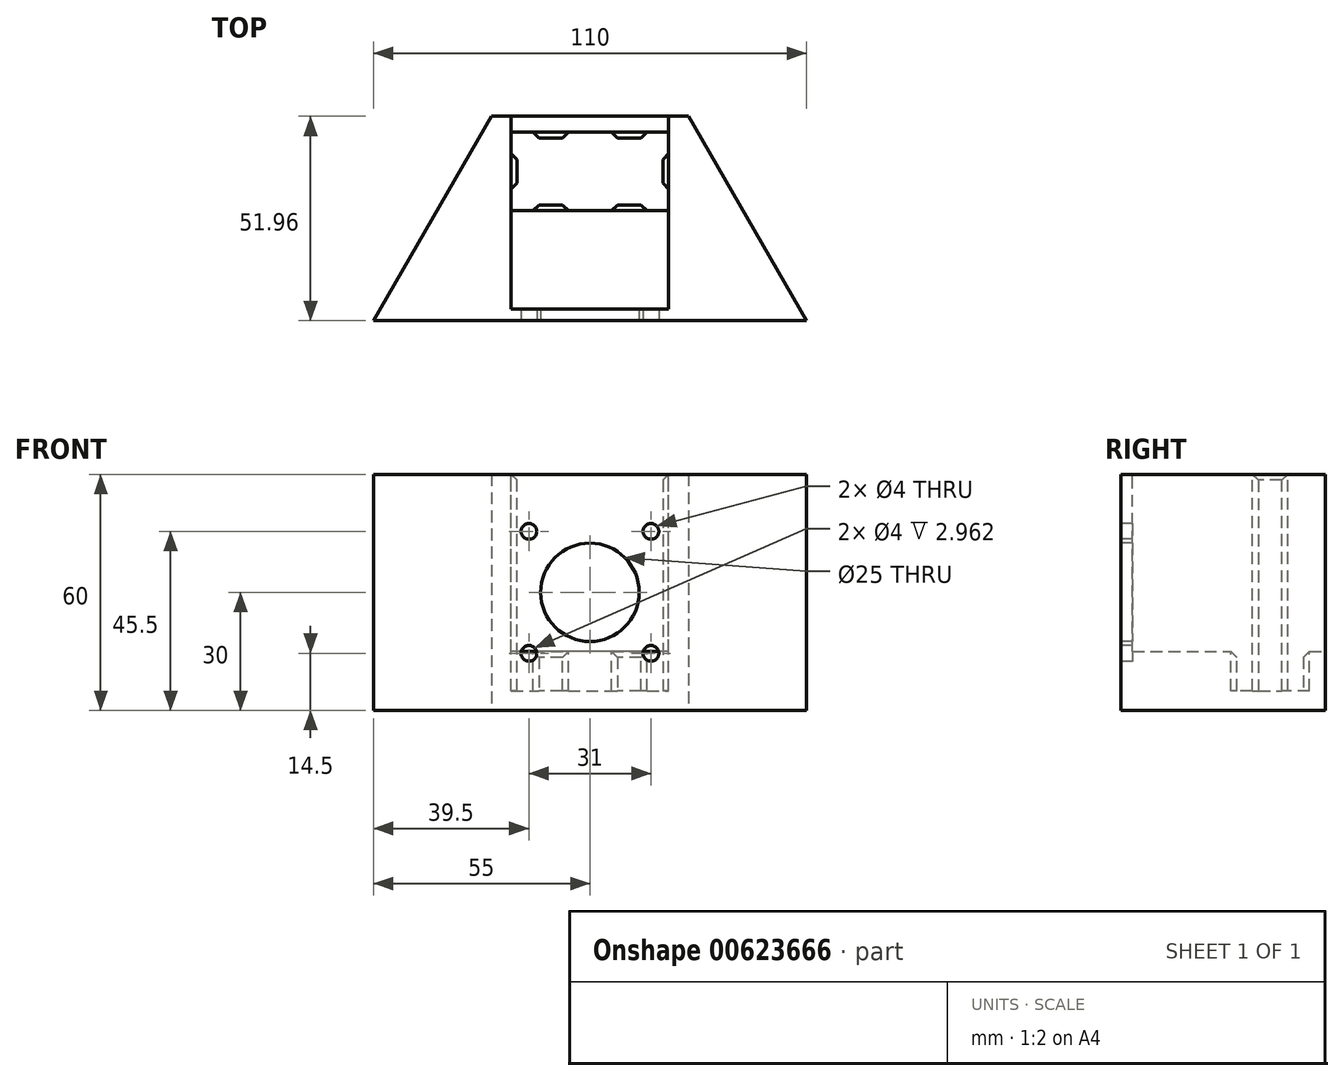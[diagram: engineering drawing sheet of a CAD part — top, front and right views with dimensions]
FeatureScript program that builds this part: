
annotation { "Feature Type Name" : "Feature", "Feature Type Description" : "" }
export const myFeature = defineFeature(function(context is Context, id is Id, definition is map)
    precondition{}
    {
        {
            var Q0;
            Q0=qCreatedBy(makeId("Top.planeOp"),FACE);
            var sketch = newSketch(context, id + "F0", { "sketchPlane" : qUnion([Q0])});
            skLineSegment(sketch, "E0", {"start": v(0, 0) * mm, "end": v(30, 51.96) * mm});
            skLineSegment(sketch, "E1", {"start": v(30, 51.96) * mm, "end": v(80, 51.96) * mm});
            skLineSegment(sketch, "E2", {"start": v(80, 51.96) * mm, "end": v(110, 0) * mm});
            skLineSegment(sketch, "E3", {"start": v(110, 0) * mm, "end": v(0, 0) * mm});
            skSolve(sketch);
        }
        {
            var Q0;
            Q0=makeQuery(id+"F0.imprint","IMPRINT",FACE,{"disambiguationData":[TD([[makeQuery(id+"F0.imprint","IMPRINT",EDGE,{"derivedFrom":sQuery(id+"F0.wireOp",EDGE,"E0")}),-1.0]])]});
            extrude(context, id + "F1", {"entities" : qUnion([Q0]), "depth" : 60 * mm, "offsetDistance" : 25 * mm});
        }
        {
            var Q0;
            Q0=makeQuery(id+"F1.opExtrude","CAP_FACE",FACE,{"disambiguationData":[OSD([sQuery(id+"F0.wireOp",EDGE,"E0"),sQuery(id+"F0.wireOp",EDGE,"E1"),sQuery(id+"F0.wireOp",EDGE,"E2"),sQuery(id+"F0.wireOp",EDGE,"E3")])],"isStart":false});
            var sketch = newSketch(context, id + "F2", { "sketchPlane" : qUnion([Q0])});
            skLineSegment(sketch, "E4.bottom", {"start": v(35, 47.96) * mm, "end": v(75, 47.96) * mm});
            skLineSegment(sketch, "E4.top", {"start": v(35, 27.96) * mm, "end": v(75, 27.96) * mm});
            skLineSegment(sketch, "E4.left", {"start": v(35, 47.96) * mm, "end": v(35, 27.96) * mm});
            skLineSegment(sketch, "E4.right", {"start": v(75, 47.96) * mm, "end": v(75, 27.96) * mm});
            skSolve(sketch);
        }
        {
            var Q0;
            Q0=makeQuery(id+"F2.imprint","IMPRINT",FACE,{"disambiguationData":[TD([[makeQuery(id+"F2.imprint","IMPRINT",EDGE,{"derivedFrom":sQuery(id+"F2.wireOp",EDGE,"E4.bottom")}),-1.0]])]});
            extrude(context, id + "F3", {"entities" : qUnion([Q0]), "operationType" : NewBodyOperationType.REMOVE, "oppositeDirection" : true, "depth" : 55 * mm, "offsetDistance" : 25 * mm});
        }
        {
            var Q0;
            Q0=makeQuery(id+"F1.opExtrude","SWEPT_FACE",FACE,{"disambiguationData":[OSD([sQuery(id+"F0.wireOp",EDGE,"E1")])]});
            var sketch = newSketch(context, id + "F4", { "sketchPlane" : qUnion([Q0])});
            skLineSegment(sketch, "E5.0.0", {"start": v(-35, 60) * mm, "end": v(-75, 60) * mm});
            skLineSegment(sketch, "E5.0.1", {"start": v(-75, 60) * mm, "end": v(-75, 15) * mm});
            skLineSegment(sketch, "E5.0.3", {"start": v(-35, 15) * mm, "end": v(-35, 60) * mm});
            skLineSegment(sketch, "E6", {"start": v(-75, 15) * mm, "end": v(-35, 15) * mm});
            skPoint(sketch, "E7.orphan", {"position": v(-35, 5) * mm});
            skPoint(sketch, "E8.orphan", {"position": v(-75, 5) * mm});
            skSolve(sketch);
        }
        {
            var Q0;
            Q0 = qSketchRegion(id + "F4", true);
            extrude(context, id + "F5", {"entities" : qUnion([Q0]), "operationType" : NewBodyOperationType.REMOVE, "endBound" : BoundingType.UP_TO_NEXT, "oppositeDirection" : true, "depth" : 25 * mm, "offsetDistance" : 25 * mm});
        }
        {
            var Q0;
            Q0=makeQuery(id+"F3.boolean.opBoolean","COPY",FACE,{"derivedFrom":makeQuery(id+"F3.opExtrude","SWEPT_FACE",FACE,{"disambiguationData":[OSD([sQuery(id+"F2.wireOp",EDGE,"E4.top")])]})});
            var sketch = newSketch(context, id + "F6", { "sketchPlane" : qUnion([Q0])});
            skLineSegment(sketch, "E9.0", {"start": v(-35, 60) * mm, "end": v(-75, 60) * mm});
            skLineSegment(sketch, "E10.0", {"start": v(-75, 60) * mm, "end": v(-75, 15) * mm});
            skLineSegment(sketch, "E11.0", {"start": v(-75, 15) * mm, "end": v(-35, 15) * mm});
            skLineSegment(sketch, "E12.0", {"start": v(-35, 15) * mm, "end": v(-35, 60) * mm});
            skSolve(sketch);
        }
        {
            var Q0;
            Q0=makeQuery(id+"F6.imprint","IMPRINT",FACE,{"disambiguationData":[TD([[makeQuery(id+"F6.imprint","IMPRINT",EDGE,{"derivedFrom":sQuery(id+"F6.wireOp",EDGE,"E9.0")}),1.0]])]});
            extrude(context, id + "F7", {"entities" : qUnion([Q0]), "operationType" : NewBodyOperationType.REMOVE, "oppositeDirection" : true, "depth" : 25 * mm, "offsetDistance" : 25 * mm});
        }
        {
            var Q0;
            Q0=makeQuery(id+"F1.opExtrude","SWEPT_FACE",FACE,{"disambiguationData":[OSD([sQuery(id+"F0.wireOp",EDGE,"E3")])]});
            var sketch = newSketch(context, id + "F8", { "sketchPlane" : qUnion([Q0])});
            skCircle(sketch, "E13", {"center": v(55, 30) * mm, "radius": 12.5 * mm});
            skPoint(sketch, "E13.centerSnap0", {"position": v(0, 30) * mm});
            skPoint(sketch, "E13.centerSnap1", {"position": v(55, 60) * mm});
            skCircle(sketch, "E14", {"center": v(70.5, 45.5) * mm, "radius": 2 * mm});
            skCircle(sketch, "E15", {"center": v(39.5, 45.5) * mm, "radius": 2 * mm});
            skCircle(sketch, "E16", {"center": v(39.5, 14.5) * mm, "radius": 2 * mm});
            skCircle(sketch, "E17", {"center": v(70.5, 14.5) * mm, "radius": 2 * mm});
            skSolve(sketch);
        }
        {
            var Q0;
            Q0 = qSketchRegion(id + "F8", true);
            var Q1;
            Q1=makeQuery(id+"F7.boolean.opBoolean","COPY",FACE,{"derivedFrom":makeQuery(id+"F7.opExtrude","CAP_FACE",FACE,{"disambiguationData":[OSD([sQuery(id+"F6.wireOp",EDGE,"E9.0"),sQuery(id+"F6.wireOp",EDGE,"E10.0"),sQuery(id+"F6.wireOp",EDGE,"E11.0"),sQuery(id+"F6.wireOp",EDGE,"E12.0")])],"isStart":false})});
            extrude(context, id + "F9", {"entities" : qUnion([Q0]), "operationType" : NewBodyOperationType.REMOVE, "endBound" : BoundingType.UP_TO_SURFACE, "oppositeDirection" : true, "depth" : 25 * mm, "endBoundEntityFace" : qUnion([Q1]), "offsetDistance" : 25 * mm});
        }
        {
            var Q0;
            Q0=makeQuery(id+"F7.boolean.opBoolean","COPY",FACE,{"derivedFrom":makeQuery(id+"F7.opExtrude","SWEPT_FACE",FACE,{"disambiguationData":[OSD([sQuery(id+"F6.wireOp",EDGE,"E11.0")])]})});
            var sketch = newSketch(context, id + "F10", { "sketchPlane" : qUnion([Q0])});
            skLineSegment(sketch, "E18.0.0", {"start": v(75, 47.96) * mm, "end": v(75, 51.96) * mm, "construction": true});
            skLineSegment(sketch, "E18.0.1", {"start": v(75, 51.96) * mm, "end": v(35, 51.96) * mm, "construction": true});
            skLineSegment(sketch, "E18.0.2", {"start": v(35, 51.96) * mm, "end": v(35, 47.96) * mm, "construction": true});
            skLineSegment(sketch, "E18.0.3", {"start": v(35, 47.96) * mm, "end": v(75, 47.96) * mm, "construction": true});
            skLineSegment(sketch, "E19.0", {"start": v(110, 0) * mm, "end": v(0, 0) * mm, "construction": true});
            skLineSegment(sketch, "E20.0.0", {"start": v(75, 27.96) * mm, "end": v(35, 27.96) * mm, "construction": true});
            skLineSegment(sketch, "E20.0.1", {"start": v(35, 27.96) * mm, "end": v(35, 2.96) * mm, "construction": true});
            skLineSegment(sketch, "E20.0.2", {"start": v(35, 2.96) * mm, "end": v(37.56, 2.96) * mm, "construction": true});
            skLineSegment(sketch, "E20.0.3", {"start": v(37.56, 2.96) * mm, "end": v(41.44, 2.96) * mm, "construction": true});
            skLineSegment(sketch, "E20.0.4", {"start": v(41.44, 2.96) * mm, "end": v(68.56, 2.96) * mm, "construction": true});
            skLineSegment(sketch, "E20.0.5", {"start": v(68.56, 2.96) * mm, "end": v(72.44, 2.96) * mm, "construction": true});
            skLineSegment(sketch, "E20.0.6", {"start": v(72.44, 2.96) * mm, "end": v(75, 2.96) * mm, "construction": true});
            skLineSegment(sketch, "E20.0.7", {"start": v(75, 2.96) * mm, "end": v(75, 27.96) * mm, "construction": true});
            skLineSegment(sketch, "E21.bottom", {"start": v(40.5, 47.96) * mm, "end": v(49.5, 47.96) * mm});
            skLineSegment(sketch, "E21.top", {"start": v(40.5, 46.46) * mm, "end": v(49.5, 46.46) * mm});
            skLineSegment(sketch, "E21.left", {"start": v(40.5, 47.96) * mm, "end": v(40.5, 46.46) * mm});
            skLineSegment(sketch, "E21.right", {"start": v(49.5, 47.96) * mm, "end": v(49.5, 46.46) * mm});
            skLineSegment(sketch, "E22.bottom", {"start": v(60.5, 47.96) * mm, "end": v(69.5, 47.96) * mm});
            skLineSegment(sketch, "E22.top", {"start": v(60.5, 46.46) * mm, "end": v(69.5, 46.46) * mm});
            skLineSegment(sketch, "E22.left", {"start": v(60.5, 47.96) * mm, "end": v(60.5, 46.46) * mm});
            skLineSegment(sketch, "E22.right", {"start": v(69.5, 47.96) * mm, "end": v(69.5, 46.46) * mm});
            skLineSegment(sketch, "E23.0", {"start": v(35, 51.96) * mm, "end": v(35, 2.96) * mm, "construction": true});
            skLineSegment(sketch, "E24.0", {"start": v(75, 51.96) * mm, "end": v(75, 2.96) * mm, "construction": true});
            skLineSegment(sketch, "E25.bottom", {"start": v(40.5, 27.96) * mm, "end": v(49.5, 27.96) * mm});
            skLineSegment(sketch, "E25.top", {"start": v(40.5, 29.46) * mm, "end": v(49.5, 29.46) * mm});
            skLineSegment(sketch, "E25.left", {"start": v(40.5, 27.96) * mm, "end": v(40.5, 29.46) * mm});
            skLineSegment(sketch, "E25.right", {"start": v(49.5, 27.96) * mm, "end": v(49.5, 29.46) * mm});
            skLineSegment(sketch, "E26.bottom", {"start": v(69.5, 27.96) * mm, "end": v(60.5, 27.96) * mm});
            skLineSegment(sketch, "E26.top", {"start": v(69.5, 29.46) * mm, "end": v(60.5, 29.46) * mm});
            skLineSegment(sketch, "E26.left", {"start": v(69.5, 27.96) * mm, "end": v(69.5, 29.46) * mm});
            skLineSegment(sketch, "E26.right", {"start": v(60.5, 27.96) * mm, "end": v(60.5, 29.46) * mm});
            skLineSegment(sketch, "E27.bottom", {"start": v(35, 42.46) * mm, "end": v(36.5, 42.46) * mm});
            skLineSegment(sketch, "E27.top", {"start": v(35, 33.46) * mm, "end": v(36.5, 33.46) * mm});
            skLineSegment(sketch, "E27.left", {"start": v(35, 42.46) * mm, "end": v(35, 33.46) * mm});
            skLineSegment(sketch, "E27.right", {"start": v(36.5, 42.46) * mm, "end": v(36.5, 33.46) * mm});
            skLineSegment(sketch, "E28.bottom", {"start": v(75, 42.46) * mm, "end": v(73.5, 42.46) * mm});
            skLineSegment(sketch, "E28.top", {"start": v(75, 33.46) * mm, "end": v(73.5, 33.46) * mm});
            skLineSegment(sketch, "E28.left", {"start": v(75, 42.46) * mm, "end": v(75, 33.46) * mm});
            skLineSegment(sketch, "E28.right", {"start": v(73.5, 42.46) * mm, "end": v(73.5, 33.46) * mm});
            skSolve(sketch);
        }
        {
            var Q0;
            Q0 = qSketchRegion(id + "F10", true);
            extrude(context, id + "F11", {"entities" : qUnion([Q0]), "operationType" : NewBodyOperationType.ADD, "endBound" : BoundingType.UP_TO_NEXT, "oppositeDirection" : true, "depth" : 25 * mm, "offsetDistance" : 25 * mm});
        }
        {
            var Q0;
            Q0=makeQuery(id+"F11.opExtrude","CAP_FACE",FACE,{"disambiguationData":[OSD([sQuery(id+"F10.wireOp",EDGE,"E28.bottom"),sQuery(id+"F10.wireOp",EDGE,"E28.top"),sQuery(id+"F10.wireOp",EDGE,"E28.left"),sQuery(id+"F10.wireOp",EDGE,"E28.right")])],"isStart":true});
            var Q1;
            Q1=makeQuery(id+"F11.opExtrude","CAP_FACE",FACE,{"disambiguationData":[OSD([sQuery(id+"F10.wireOp",EDGE,"E27.bottom"),sQuery(id+"F10.wireOp",EDGE,"E27.top"),sQuery(id+"F10.wireOp",EDGE,"E27.left"),sQuery(id+"F10.wireOp",EDGE,"E27.right")])],"isStart":true});
            var Q2;
            Q2=makeQuery(id+"F1.opExtrude","CAP_FACE",FACE,{"disambiguationData":[OSD([sQuery(id+"F0.wireOp",EDGE,"E0"),sQuery(id+"F0.wireOp",EDGE,"E1"),sQuery(id+"F0.wireOp",EDGE,"E2"),sQuery(id+"F0.wireOp",EDGE,"E3")])],"isStart":false});
            extrude(context, id + "F12", {"entities" : qUnion([Q0, Q1]), "operationType" : NewBodyOperationType.ADD, "endBound" : BoundingType.UP_TO_SURFACE, "depth" : 25 * mm, "endBoundEntityFace" : qUnion([Q2]), "offsetDistance" : 25 * mm});
        }
        {
            var Q0;
            {var subQ0=sQuery(id+"F10.wireOp",EDGE,"E27.right");var subQ1=sQuery(id+"F10.wireOp",EDGE,"E27.top");Q0=makeQuery(id+"F12.boolean.opBoolean","MERGE",EDGE,{"derivedFrom":[makeQuery(id+"F11.opExtrude","SWEPT_EDGE",EDGE,{"disambiguationData":[OSD([subQ1,subQ0])]}),makeQuery(id+"F12.opExtrude","SWEPT_EDGE",EDGE,{"disambiguationData":[OSD([subQ1,subQ0])]})]});}
            var Q1;
            Q1=makeQuery(id+"F12.opExtrude","CAP_EDGE",EDGE,{"disambiguationData":[OSD([sQuery(id+"F10.wireOp",EDGE,"E28.right")])],"isStart":false});
            var Q2;
            {var subQ0=sQuery(id+"F10.wireOp",EDGE,"E28.right");var subQ1=sQuery(id+"F10.wireOp",EDGE,"E28.bottom");Q2=makeQuery(id+"F12.boolean.opBoolean","MERGE",EDGE,{"derivedFrom":[makeQuery(id+"F11.opExtrude","SWEPT_EDGE",EDGE,{"disambiguationData":[OSD([subQ1,subQ0])]}),makeQuery(id+"F12.opExtrude","SWEPT_EDGE",EDGE,{"disambiguationData":[OSD([subQ1,subQ0])]})]});}
            var Q3;
            Q3=makeQuery(id+"F12.opExtrude","CAP_EDGE",EDGE,{"disambiguationData":[OSD([sQuery(id+"F10.wireOp",EDGE,"E27.right")])],"isStart":false});
            var Q4;
            {var subQ0=sQuery(id+"F10.wireOp",EDGE,"E27.right");var subQ1=sQuery(id+"F10.wireOp",EDGE,"E27.bottom");Q4=makeQuery(id+"F12.boolean.opBoolean","MERGE",EDGE,{"derivedFrom":[makeQuery(id+"F11.opExtrude","SWEPT_EDGE",EDGE,{"disambiguationData":[OSD([subQ1,subQ0])]}),makeQuery(id+"F12.opExtrude","SWEPT_EDGE",EDGE,{"disambiguationData":[OSD([subQ1,subQ0])]})]});}
            var Q5;
            {var subQ0=sQuery(id+"F10.wireOp",EDGE,"E28.right");var subQ1=sQuery(id+"F10.wireOp",EDGE,"E28.top");Q5=makeQuery(id+"F12.boolean.opBoolean","MERGE",EDGE,{"derivedFrom":[makeQuery(id+"F11.opExtrude","SWEPT_EDGE",EDGE,{"disambiguationData":[OSD([subQ1,subQ0])]}),makeQuery(id+"F12.opExtrude","SWEPT_EDGE",EDGE,{"disambiguationData":[OSD([subQ1,subQ0])]})]});}
            var Q6;
            Q6=makeQuery(id+"F11.opExtrude","CAP_EDGE",EDGE,{"disambiguationData":[OSD([sQuery(id+"F10.wireOp",EDGE,"E26.top")])],"isStart":true});
            var Q7;
            Q7=makeQuery(id+"F11.opExtrude","SWEPT_EDGE",EDGE,{"disambiguationData":[OSD([sQuery(id+"F10.wireOp",EDGE,"E26.top"),sQuery(id+"F10.wireOp",EDGE,"E26.left")])]});
            var Q8;
            Q8=makeQuery(id+"F11.opExtrude","SWEPT_EDGE",EDGE,{"disambiguationData":[OSD([sQuery(id+"F10.wireOp",EDGE,"E26.top"),sQuery(id+"F10.wireOp",EDGE,"E26.right")])]});
            var Q9;
            Q9=makeQuery(id+"F11.opExtrude","SWEPT_EDGE",EDGE,{"disambiguationData":[OSD([sQuery(id+"F10.wireOp",EDGE,"E25.top"),sQuery(id+"F10.wireOp",EDGE,"E25.right")])]});
            var Q10;
            Q10=makeQuery(id+"F11.opExtrude","CAP_EDGE",EDGE,{"disambiguationData":[OSD([sQuery(id+"F10.wireOp",EDGE,"E25.top")])],"isStart":true});
            var Q11;
            Q11=makeQuery(id+"F11.opExtrude","SWEPT_EDGE",EDGE,{"disambiguationData":[OSD([sQuery(id+"F10.wireOp",EDGE,"E21.top"),sQuery(id+"F10.wireOp",EDGE,"E21.left")])]});
            var Q12;
            Q12=makeQuery(id+"F11.opExtrude","CAP_EDGE",EDGE,{"disambiguationData":[OSD([sQuery(id+"F10.wireOp",EDGE,"E21.top")])],"isStart":true});
            var Q13;
            Q13=makeQuery(id+"F11.opExtrude","SWEPT_EDGE",EDGE,{"disambiguationData":[OSD([sQuery(id+"F10.wireOp",EDGE,"E22.top"),sQuery(id+"F10.wireOp",EDGE,"E22.left")])]});
            var Q14;
            Q14=makeQuery(id+"F11.opExtrude","CAP_EDGE",EDGE,{"disambiguationData":[OSD([sQuery(id+"F10.wireOp",EDGE,"E22.top")])],"isStart":true});
            var Q15;
            Q15=makeQuery(id+"F11.opExtrude","SWEPT_EDGE",EDGE,{"disambiguationData":[OSD([sQuery(id+"F10.wireOp",EDGE,"E21.top"),sQuery(id+"F10.wireOp",EDGE,"E21.right")])]});
            var Q16;
            Q16=makeQuery(id+"F11.opExtrude","SWEPT_EDGE",EDGE,{"disambiguationData":[OSD([sQuery(id+"F10.wireOp",EDGE,"E25.top"),sQuery(id+"F10.wireOp",EDGE,"E25.left")])]});
            var Q17;
            Q17=makeQuery(id+"F11.opExtrude","SWEPT_EDGE",EDGE,{"disambiguationData":[OSD([sQuery(id+"F10.wireOp",EDGE,"E22.top"),sQuery(id+"F10.wireOp",EDGE,"E22.right")])]});
            chamfer(context, id + "F13", {"entities" : qUnion([Q0, Q1, Q2, Q3, Q4, Q5, Q6, Q7, Q8, Q9, Q10, Q11, Q12, Q13, Q14, Q15, Q16, Q17]), "width" : 1.5 * mm, "tangentPropagation" : true});
        }
    });
